# Revit family: BuzziFloat
name_source: partatom
category: Furniture
units: mm (PartAtom-declared; Revit-internal decimal feet)

## family parameters
Always vertical = Yes
Cut with Voids When Loaded = No
OmniClass Number = 23.40.20.00
OmniClass Title = General Furniture and Specialties
Room Calculation Point = No
Shared = No
Work Plane-Based = No

## types (6) — shared parameters
4 Star Base = BuzziFloat - FloatCross Base
4 Star Base Caster = BuzziFloat - Base Hardware : Casters
4 Star Base Glide = BuzziFloat - Base Hardware : Glides
Wood Base = BuzziFloat - Float Base : BuzziFloat Wood Base

## per-type parameters (varying)
| type | 2D Base Visibility | 2D Caster Visibility | 4 Star Base Leg Height | Base Hardware Type | Base Hardware Visibility | Base Type | Cushions | Hardware Value |
| Float CrossPlus with Upholstery | No | Yes | 0' - 2 9/16" | BuzziFloat - Base Hardware : Casters | Yes | BuzziFloat - FloatCross Base | Yes | 0 |
| Float Cross Base with Upholstery | No | No | 0' - 0 1/4" | BuzziFloat - Base Hardware : Glides | Yes | BuzziFloat - FloatCross Base | Yes | 1 |
| Float Base with Upholstery | Yes | No | 0' - 0 1/4" | BuzziFloat - Base Hardware : Glides | No | BuzziFloat - Float Base : BuzziFloat Wood Base | Yes | 2 |
| Float CrossPlus Base without Upholstery | No | Yes | 0' - 2 9/16" | BuzziFloat - Base Hardware : Casters | Yes | BuzziFloat - FloatCross Base | No | 0 |
| Float Cross Base without Upholstery | No | No | 0' - 0 1/4" | BuzziFloat - Base Hardware : Glides | Yes | BuzziFloat - FloatCross Base | No | 1 |
| Float Base without Upholstery | Yes | No | 0' - 0 1/4" | BuzziFloat - Base Hardware : Glides | No | BuzziFloat - Float Base : BuzziFloat Wood Base | No | 2 |

## geometry (parser evidence)
native form markers: Sweep x12
no freeform markers — native parametric forms only
